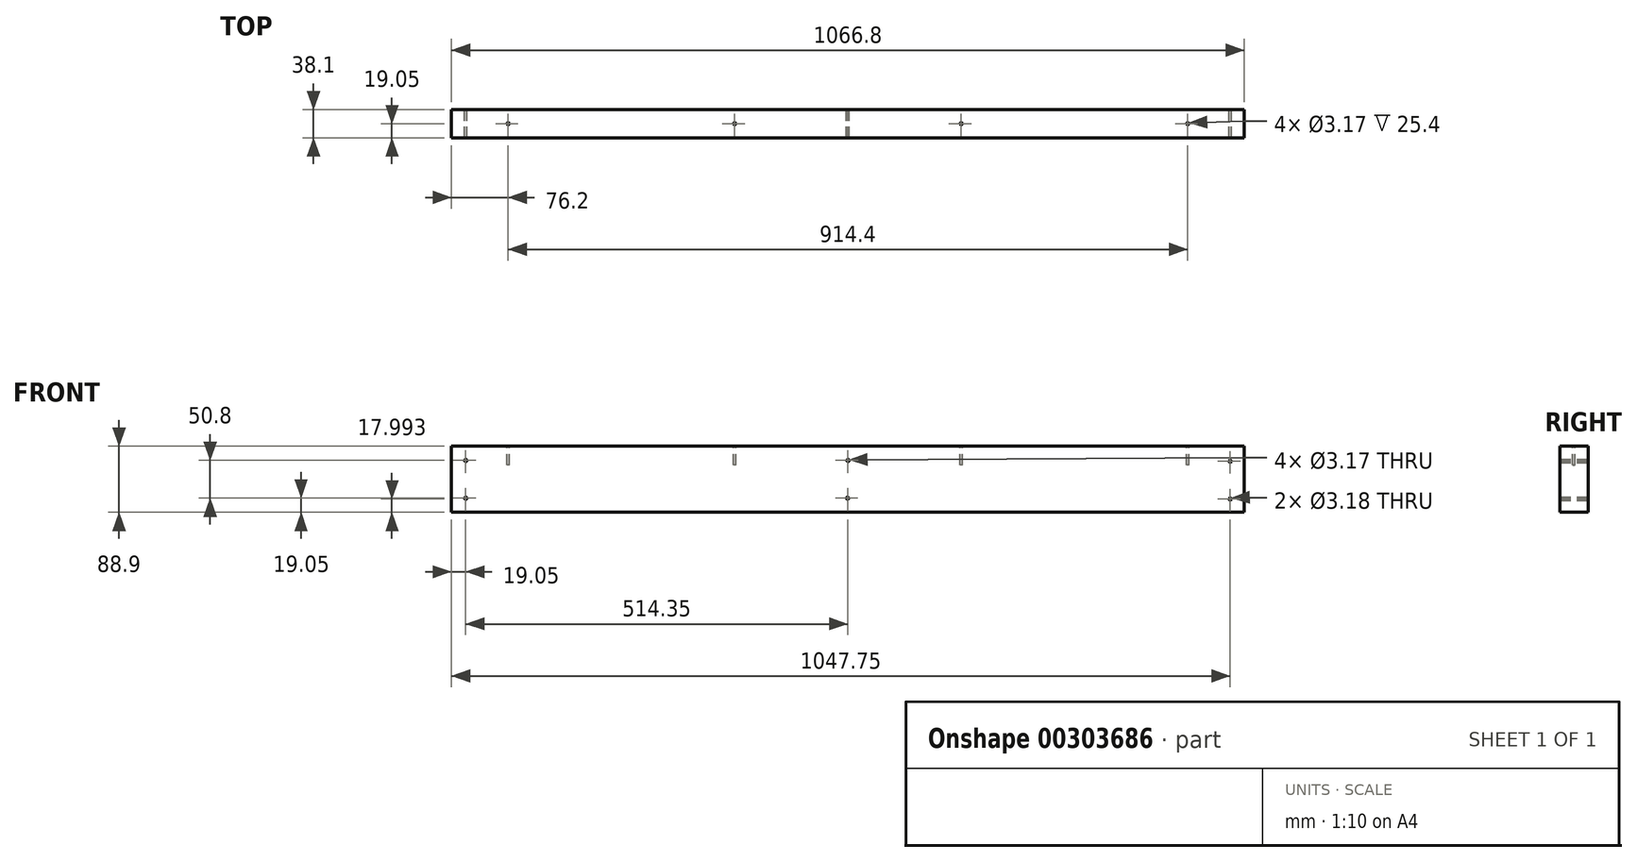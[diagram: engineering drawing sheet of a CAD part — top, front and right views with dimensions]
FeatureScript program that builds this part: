
annotation { "Feature Type Name" : "Feature", "Feature Type Description" : "" }
export const myFeature = defineFeature(function(context is Context, id is Id, definition is map)
    precondition{}
    {
        {
            var Q0;
            Q0=qCreatedBy(makeId("Front.planeOp"),FACE);
            var sketch = newSketch(context, id + "F0", { "sketchPlane" : qUnion([Q0])});
            skLineSegment(sketch, "E0.bottom", {"start": v(0, 0) * mm, "end": v(1066.8, 0) * mm});
            skLineSegment(sketch, "E0.top", {"start": v(0, -88.9) * mm, "end": v(1066.8, -88.9) * mm});
            skLineSegment(sketch, "E0.left", {"start": v(0, 0) * mm, "end": v(0, -88.9) * mm});
            skLineSegment(sketch, "E0.right", {"start": v(1066.8, 0) * mm, "end": v(1066.8, -88.9) * mm});
            skSolve(sketch);
        }
        {
            var Q0;
            Q0 = qSketchRegion(id + "F0", true);
            extrude(context, id + "F1", {"entities" : qUnion([Q0]), "depth" : 38.1 * mm});
        }
        {
            var Q0;
            Q0=qCreatedBy(makeId("Top.planeOp"),FACE);
            var sketch = newSketch(context, id + "F2", { "sketchPlane" : qUnion([Q0])});
            skCircle(sketch, "E1", {"center": v(76.2, -19.05) * mm, "radius": 1.59 * mm});
            skCircle(sketch, "E2.1.0.0", {"center": v(381, -19.05) * mm, "radius": 1.59 * mm});
            skCircle(sketch, "E2.2.0.0", {"center": v(685.8, -19.05) * mm, "radius": 1.59 * mm});
            skCircle(sketch, "E2.3.0.0", {"center": v(990.6, -19.05) * mm, "radius": 1.59 * mm});
            skLineSegment(sketch, "E2.direction1", {"start": v(76.2, -19.05) * mm, "end": v(381, -19.05) * mm, "construction": true});
            skSolve(sketch);
        }
        {
            var Q0;
            Q0=makeQuery(id+"F2.imprint","IMPRINT",FACE,{"disambiguationData":[TD([[makeQuery(id+"F2.imprint","IMPRINT",EDGE,{"derivedFrom":sQuery(id+"F2.wireOp",EDGE,"E1")}),1.0]])]});
            var Q1;
            Q1=makeQuery(id+"F2.imprint","IMPRINT",FACE,{"disambiguationData":[TD([[makeQuery(id+"F2.imprint","IMPRINT",EDGE,{"derivedFrom":sQuery(id+"F2.wireOp",EDGE,"E2.1.0.0")}),1.0]])]});
            var Q2;
            Q2=makeQuery(id+"F2.imprint","IMPRINT",FACE,{"disambiguationData":[TD([[makeQuery(id+"F2.imprint","IMPRINT",EDGE,{"derivedFrom":sQuery(id+"F2.wireOp",EDGE,"E2.2.0.0")}),1.0]])]});
            var Q3;
            Q3=makeQuery(id+"F2.imprint","IMPRINT",FACE,{"disambiguationData":[TD([[makeQuery(id+"F2.imprint","IMPRINT",EDGE,{"derivedFrom":sQuery(id+"F2.wireOp",EDGE,"E2.3.0.0")}),1.0]])]});
            extrude(context, id + "F3", {"entities" : qUnion([Q0, Q1, Q2, Q3]), "operationType" : NewBodyOperationType.REMOVE, "oppositeDirection" : true, "depth" : 25.4 * mm});
        }
        {
            var Q0;
            Q0=qCreatedBy(makeId("Front.planeOp"),FACE);
            var sketch = newSketch(context, id + "F4", { "sketchPlane" : qUnion([Q0])});
            skCircle(sketch, "E3", {"center": v(19.05, -19.05) * mm, "radius": 1.59 * mm});
            skCircle(sketch, "E4.0.1.0", {"center": v(19.05, -69.85) * mm, "radius": 1.59 * mm});
            skCircle(sketch, "E4.1.0.0", {"center": v(1047.75, -20.1) * mm, "radius": 1.59 * mm});
            skCircle(sketch, "E4.1.1.0", {"center": v(1047.75, -70.9) * mm, "radius": 1.59 * mm});
            skLineSegment(sketch, "E4.direction1", {"start": v(19.05, -19.05) * mm, "end": v(1047.75, -20.1) * mm, "construction": true});
            skLineSegment(sketch, "E4.direction2", {"start": v(19.05, -19.05) * mm, "end": v(19.05, -69.85) * mm, "construction": true});
            skSolve(sketch);
        }
        {
            var Q0;
            Q0 = qSketchRegion(id + "F4", true);
            extrude(context, id + "F5", {"entities" : qUnion([Q0]), "operationType" : NewBodyOperationType.REMOVE, "endBound" : BoundingType.THROUGH_ALL, "depth" : 25.4 * mm});
        }
        {
            var Q0;
            Q0=qCreatedBy(makeId("Front.planeOp"),FACE);
            var sketch = newSketch(context, id + "F6", { "sketchPlane" : qUnion([Q0])});
            skCircle(sketch, "E5", {"center": v(533.4, -19.05) * mm, "radius": 1.59 * mm});
            skCircle(sketch, "E6.1.0.0", {"center": v(532.98, -69.85) * mm, "radius": 1.59 * mm});
            skLineSegment(sketch, "E6.direction1", {"start": v(533.4, -19.05) * mm, "end": v(532.98, -69.85) * mm, "construction": true});
            skSolve(sketch);
        }
        {
            var Q0;
            Q0 = qSketchRegion(id + "F6", true);
            extrude(context, id + "F7", {"entities" : qUnion([Q0]), "operationType" : NewBodyOperationType.REMOVE, "endBound" : BoundingType.THROUGH_ALL, "depth" : 25.4 * mm});
        }
    });
